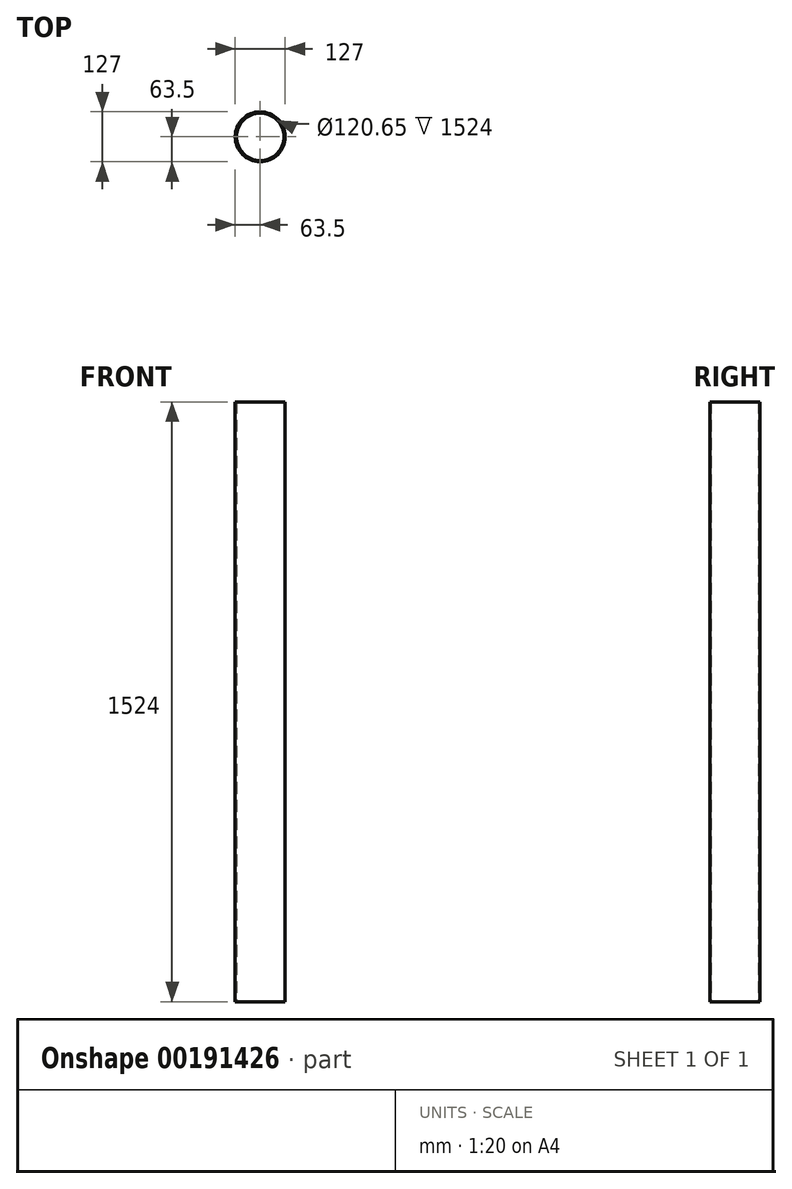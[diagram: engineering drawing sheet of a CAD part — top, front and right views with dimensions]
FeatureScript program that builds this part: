
annotation { "Feature Type Name" : "Feature", "Feature Type Description" : "" }
export const myFeature = defineFeature(function(context is Context, id is Id, definition is map)
    precondition{}
    {
        {
            var Q0;
            Q0=qCreatedBy(makeId("Top.planeOp"),FACE);
            var sketch = newSketch(context, id + "F0", { "sketchPlane" : qUnion([Q0])});
            skCircle(sketch, "E0", {"center": v(0, 0) * mm, "radius": 63.5 * mm});
            skCircle(sketch, "E1", {"center": v(0, 0) * mm, "radius": 60.33 * mm});
            skSolve(sketch);
        }
        {
            var Q0;
            Q0=makeQuery(id+"F0.imprint","IMPRINT",FACE,{"disambiguationData":[TD([[makeQuery(id+"F0.imprint","IMPRINT",EDGE,{"derivedFrom":sQuery(id+"F0.wireOp",EDGE,"E0")}),1.0]])]});
            extrude(context, id + "F1", {"entities" : qUnion([Q0]), "depth" : 1524 * mm});
        }
    });
